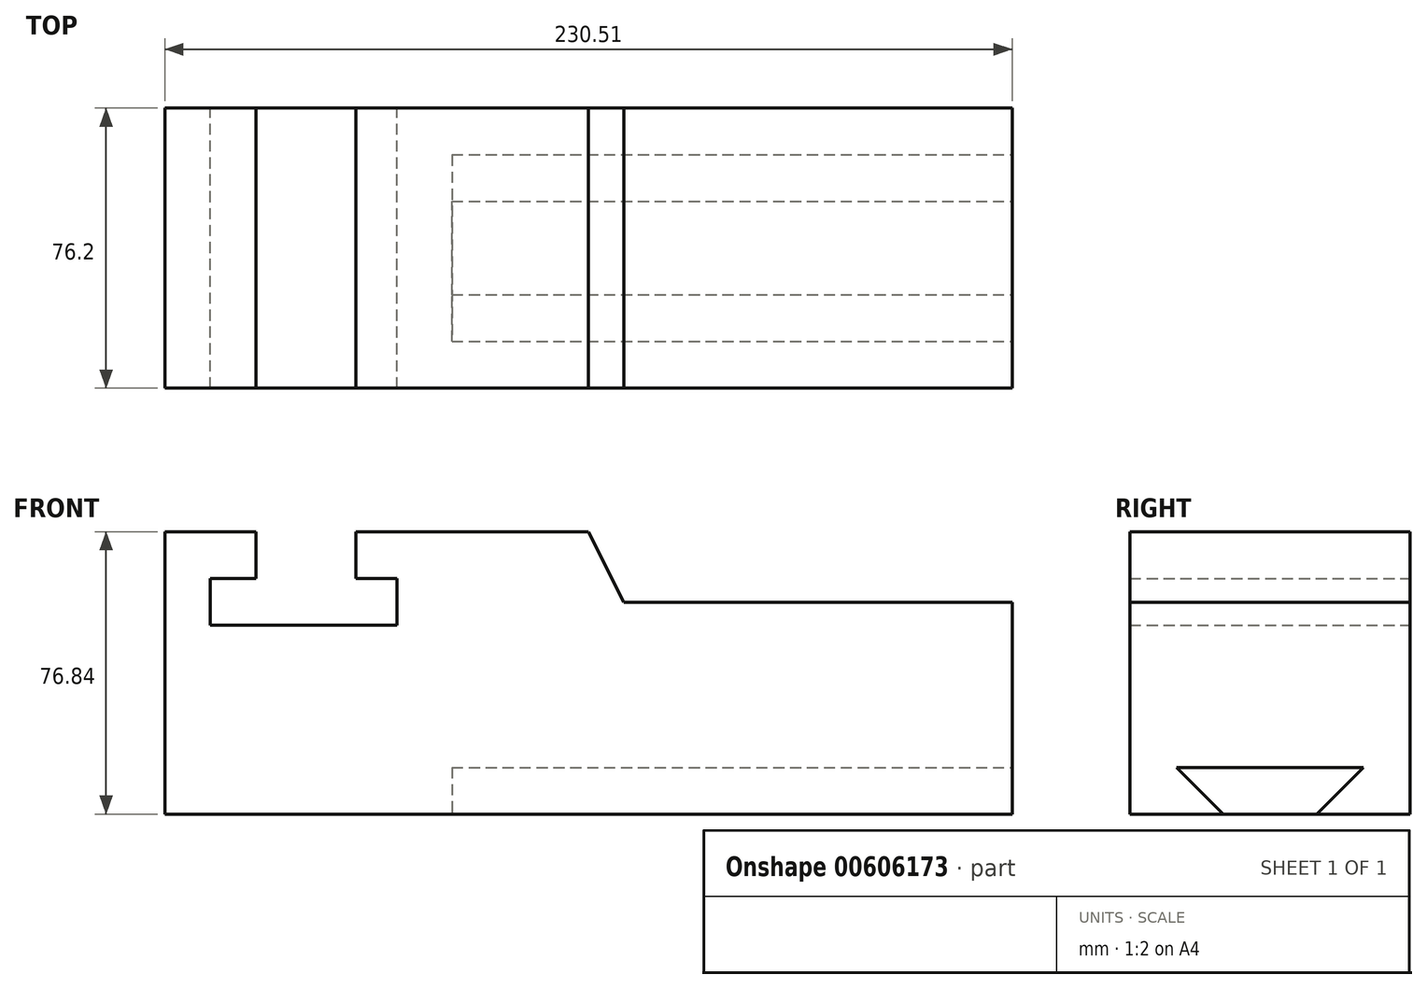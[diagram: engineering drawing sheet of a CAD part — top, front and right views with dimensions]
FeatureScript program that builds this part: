
annotation { "Feature Type Name" : "Feature", "Feature Type Description" : "" }
export const myFeature = defineFeature(function(context is Context, id is Id, definition is map)
    precondition{}
    {
        {
            var Q0;
            Q0=qCreatedBy(makeId("Front.planeOp"),FACE);
            var sketch = newSketch(context, id + "F0", { "sketchPlane" : qUnion([Q0])});
            skLineSegment(sketch, "E0", {"start": v(0, 0) * mm, "end": v(-230.51, 0) * mm});
            skLineSegment(sketch, "E1", {"start": v(-230.51, 0) * mm, "end": v(-230.51, 76.84) * mm});
            skLineSegment(sketch, "E2", {"start": v(-230.51, 76.84) * mm, "end": v(-115.26, 76.84) * mm});
            skLineSegment(sketch, "E3", {"start": v(-115.26, 76.84) * mm, "end": v(-105.65, 57.63) * mm});
            skLineSegment(sketch, "E4", {"start": v(-105.65, 57.63) * mm, "end": v(0, 57.63) * mm});
            skLineSegment(sketch, "E5", {"start": v(0, 57.63) * mm, "end": v(0, 0) * mm});
            skLineSegment(sketch, "E6", {"start": v(-230.51, 76.84) * mm, "end": v(-205.7, 76.84) * mm});
            skLineSegment(sketch, "E7", {"start": v(-205.7, 76.84) * mm, "end": v(-205.7, 64.14) * mm});
            skLineSegment(sketch, "E8", {"start": v(-205.7, 64.14) * mm, "end": v(-218.1, 64.14) * mm});
            skLineSegment(sketch, "E9", {"start": v(-218.1, 64.14) * mm, "end": v(-218.1, 51.44) * mm});
            skLineSegment(sketch, "E10", {"start": v(-218.1, 51.44) * mm, "end": v(-167.3, 51.44) * mm});
            skLineSegment(sketch, "E11", {"start": v(-167.3, 51.44) * mm, "end": v(-167.3, 64.14) * mm});
            skLineSegment(sketch, "E12", {"start": v(-167.3, 64.14) * mm, "end": v(-178.56, 64.14) * mm});
            skLineSegment(sketch, "E13", {"start": v(-178.56, 64.14) * mm, "end": v(-178.56, 76.84) * mm});
            skSolve(sketch);
        }
        {
            var Q0;
            Q0=makeQuery(id+"F0.imprint","IMPRINT",FACE,{"disambiguationData":[TD([[makeQuery(id+"F0.imprint","IMPRINT",EDGE,{"derivedFrom":sQuery(id+"F0.wireOp",EDGE,"E0")}),-1.0]])]});
            extrude(context, id + "F1", {"entities" : qUnion([Q0]), "depth" : 76.2 * mm, "offsetDistance" : 25.4 * mm});
        }
        {
            var Q0;
            Q0=makeQuery(id+"F1.opExtrude","SWEPT_FACE",FACE,{"disambiguationData":[OSD([sQuery(id+"F0.wireOp",EDGE,"E5")])]});
            var sketch = newSketch(context, id + "F2", { "sketchPlane" : qUnion([Q0])});
            skLineSegment(sketch, "E14", {"start": v(-38.1, 12.7) * mm, "end": v(-63.5, 12.7) * mm});
            skLineSegment(sketch, "E15", {"start": v(-38.1, 12.7) * mm, "end": v(-12.7, 12.7) * mm});
            skLineSegment(sketch, "E16", {"start": v(-63.5, 12.7) * mm, "end": v(-50.8, 0) * mm});
            skLineSegment(sketch, "E17", {"start": v(-12.7, 12.7) * mm, "end": v(-25.4, 0) * mm});
            skLineSegment(sketch, "E18", {"start": v(-50.8, 0) * mm, "end": v(-25.4, 0) * mm});
            skSolve(sketch);
        }
        {
            var Q0;
            Q0 = qSketchRegion(id + "F2", true);
            extrude(context, id + "F3", {"entities" : qUnion([Q0]), "operationType" : NewBodyOperationType.REMOVE, "oppositeDirection" : true, "depth" : 152.4 * mm, "offsetDistance" : 25.4 * mm});
        }
    });
